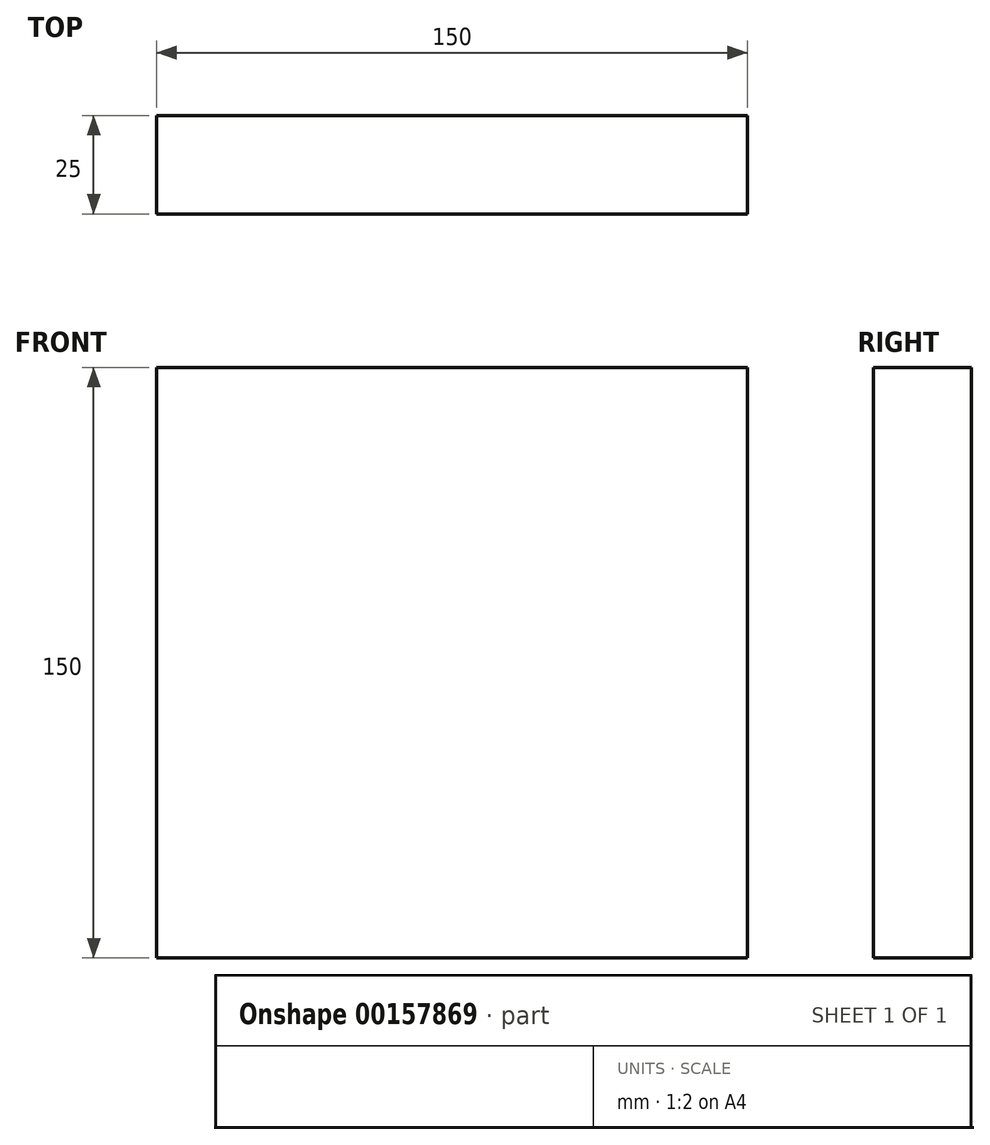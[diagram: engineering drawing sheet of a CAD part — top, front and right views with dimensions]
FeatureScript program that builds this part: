
annotation { "Feature Type Name" : "Feature", "Feature Type Description" : "" }
export const myFeature = defineFeature(function(context is Context, id is Id, definition is map)
    precondition{}
    {
        {
            var Q0;
            Q0=qCreatedBy(makeId("Right.planeOp"),FACE);
            var sketch = newSketch(context, id + "F0", { "sketchPlane" : qUnion([Q0])});
            skLineSegment(sketch, "E0.bottom", {"start": v(12.5, 75) * mm, "end": v(-12.5, 75) * mm});
            skLineSegment(sketch, "E0.top", {"start": v(12.5, -75) * mm, "end": v(-12.5, -75) * mm});
            skLineSegment(sketch, "E0.left", {"start": v(12.5, 75) * mm, "end": v(12.5, -75) * mm});
            skLineSegment(sketch, "E0.right", {"start": v(-12.5, 75) * mm, "end": v(-12.5, -75) * mm});
            skPoint(sketch, "E0.middle", {"position": v(0, 0) * mm});
            skSolve(sketch);
        }
        {
            var Q0;
            Q0 = qSketchRegion(id + "F0", true);
            extrude(context, id + "F1", {"entities" : qUnion([Q0]), "endBound" : BoundingType.SYMMETRIC, "depth" : 150 * mm});
        }
    });
